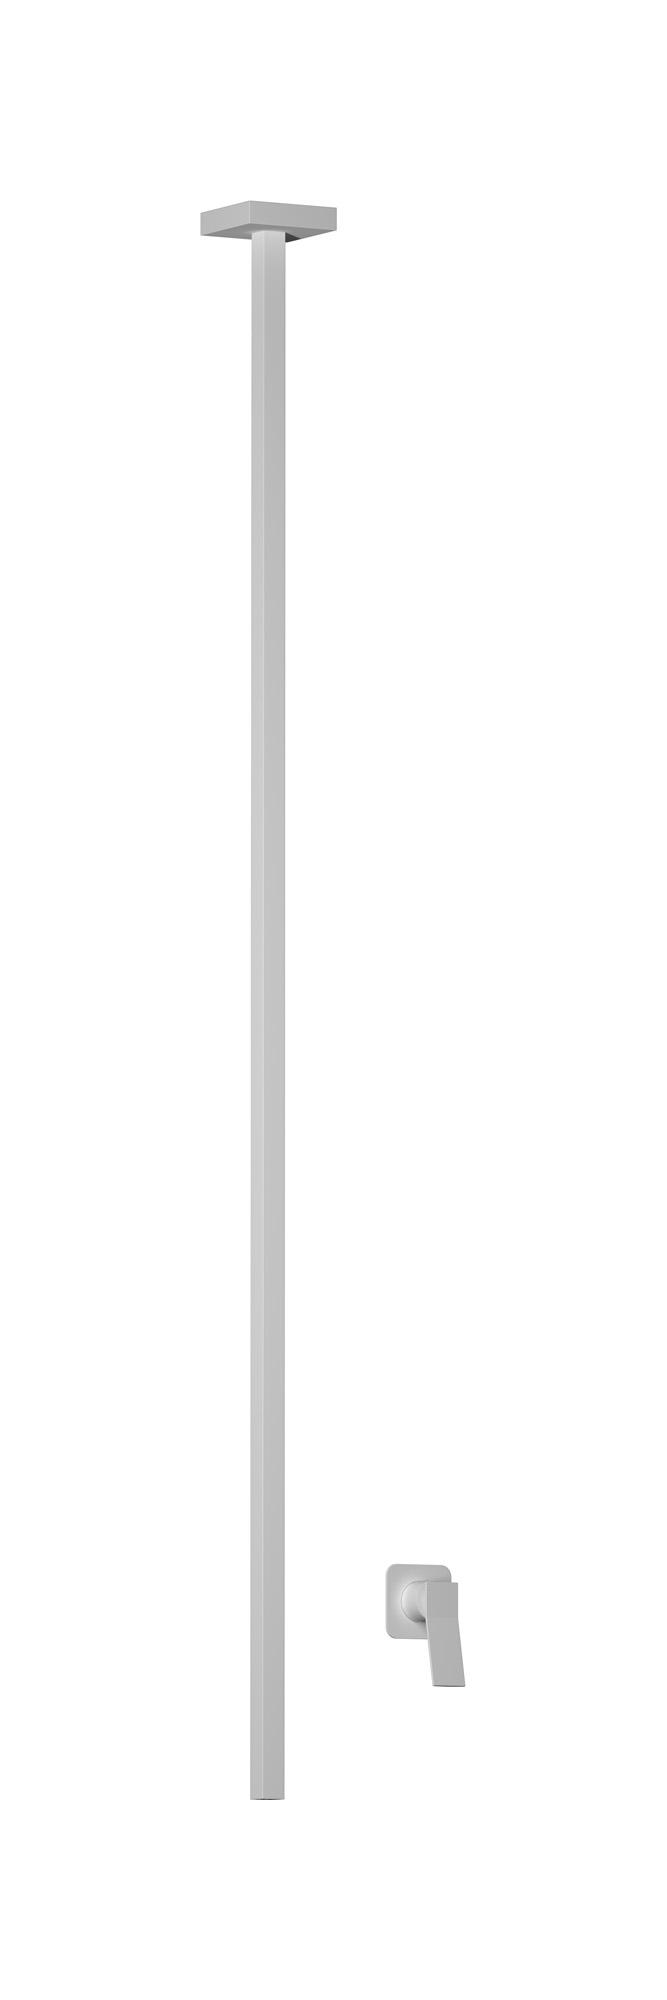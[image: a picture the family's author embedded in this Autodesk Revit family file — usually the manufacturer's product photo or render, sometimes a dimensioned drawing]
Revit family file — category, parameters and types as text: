
# Revit family: WA210
name_source: partatom
category: Apparecchi idraulici
units: mm (PartAtom-declared; Revit-internal decimal feet)

## family parameters
Basato su piano di lavoro = No
Condiviso = No
Mantieni orientamento annotazione = No
Numero OmniClass = 23.45.55.17
Punto di calcolo locali = No
Quota connettore circolare = Usa diametro
Sempre verticale = Sì
Taglio con vuoti quando caricato = No
Tipo di parte = Normale
Titolo OmniClass = Mixing Faucets

## types (4) — shared parameters
Cold water inlet = 10 mm  [stored 0.0328084 ft]
Commenti sul tipo = Ceiling spout with wall mounted mixer
Connessione CW = No
Connessione HW = No
Connessione di scarico = No
Connessione di ventilazione = No
Descrizione = Ceiling spout with wall mounted mixer
Hot water inlet = 10 mm  [stored 0.0328084 ft]
Produttore = IB Rubinetterie S.p.A.
URL = https://www.weareib.it
zero-valued in all types: Prospetto di default

## per-type parameters (varying)
| type | Finishes surface | Immagine tipo | Modello |
| Chrome | IB_Chrome | WA210CC.jpg | WA210CC |
| Brushed nickel | IB_Brushed nickel | WA210SS.jpg | WA210SS |
| Matt white | IB_matt white | WA210BO.jpg | WA210BO |
| Matt black | IB_matt black | WA210NP.jpg | WA210NP |

note: [stored X ft] marks values corroborated as IEEE doubles in the binary element streams (Revit-internal decimal feet)
